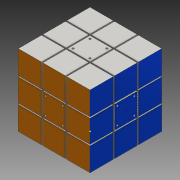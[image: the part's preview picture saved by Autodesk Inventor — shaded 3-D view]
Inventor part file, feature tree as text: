
AUTODESK INVENTOR PART (.ipt)
format: ipt  version: 2016 (Build 200138000, 138)  size: 409,088 bytes
history: native  units: mm
features: sketch x8, extrude x7, mirror x5, pattern_circular x5, plane x4, other x1, projected_geometry x1
ambient origin geometry x8: Origin, YZ Plane, XZ Plane, XY Plane, X Axis, Y Axis, Z Axis, Center Point
bodies: 实体1 (feature_tree)
feature tree (31):
  extrude  "拉伸1"  Depth=57.0mm TaperAngle=0.0deg
  extrude  "拉伸2"  Depth=1.0mm
  mirror  "镜像1"
  extrude  "拉伸3"  Depth=18.5mm
  plane  "工作平面1"
  mirror  "镜像2"
  pattern_circular  "环形阵列1"  Count=4 Angle=360.0deg
  pattern_circular  "环形阵列2"  Count=4 Angle=360.0deg
  extrude  "拉伸4"  Depth=1.0mm TaperAngle=360.0deg
  pattern_circular  "环形阵列3"  [2 undecoded]
  extrude  "拉伸5"  Depth=1.0mm
  mirror  "镜像3"
  extrude  "拉伸6"  Depth=18.5mm
  mirror  "镜像4"
  extrude  "拉伸7"  Depth=4.0mm TaperAngle=0.0deg
  mirror  "镜像5"
  pattern_circular  "环形阵列4"  [2 undecoded]
  sketch  "草图8"  dims[d23=1.0mm d24=18.5mm d25=1.0mm d26=18.5mm d27=60.0mm d28=0.0mm d29=1.0mm d30=0.0mm d31=19.0mm d32=1.5mm d33=1.5mm d34=4.0mm d35=0.0mm d36=40.0mm d37=360.0deg d39=40.0mm d40=360.0deg]
  other  "工作轴4"
  pattern_circular  "环形阵列5"  [2 undecoded]
  sketch  "草图1"  dims[d0=57.0mm d1=57.0mm d2=0.0mm]
  sketch  "草图2"  dims[d3=18.5mm d4=1.0mm]
  projected_geometry  "投影回路1"
  sketch  "草图3"  dims[d5=1.0mm d6=18.5mm]
  sketch  "草图4"  dims[d7=1.0mm d8=0.0mm]
  sketch  "草图5"  dims[d9=1.0mm d10=0.0mm]
  plane  "工作平面2"
  sketch  "草图6"  dims[d11=28.5mm d12=40.0mm d13=360.0deg d15=40.0mm d16=360.0deg]
  plane  "工作平面3"
  sketch  "草图7"  dims[d18=1.0mm d19=0.0mm d20=40.0mm d21=360.0deg]
  plane  "工作平面4"
note: 6 required parameter values undecoded (feature->parameter linkage not recoverable at this tier; creation-order binding heuristic only, values carry confidence <= 0.55)
